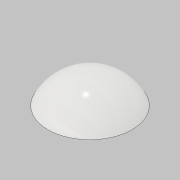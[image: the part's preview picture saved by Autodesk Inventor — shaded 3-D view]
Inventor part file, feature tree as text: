
AUTODESK INVENTOR PART (.ipt)
format: ipt  version: 2019.2 (Build 232265000, 265)  size: 482,816 bytes
history: native  units: mm
features: sketch x4, revolve x3, extrude x2, shell x1, plane x1, other x1, fillet x1
ambient origin geometry x8: Origin, YZ Plane, XZ Plane, XY Plane, X Axis, Y Axis, Z Axis, Center Point
bodies: Volumenkörper1 (feature_tree)
feature tree (13):
  shell  "ShellLower.ipt"  Thickness=10.0mm
  revolve  "Umdrehung1"
  revolve  "Umdrehung2"
  revolve  "Umdrehung3"
  plane  "Arbeitsebene1"
  other  "Trennen1"
  sketch  "Skizze2"  dims[d3=180.0deg d4=-26.0mm d5=46.0mm]
  extrude  "Extrusion1"  Depth=2.0mm
  extrude  "Extrusion2"  [1 undecoded]
  fillet  "Rundung1"  Radius=46.0mm
  sketch  "Skizze1"  dims[d1=120.0mm d2=2.0mm]
  sketch  "Skizze3"  dims[d6=7.0mm]
  sketch  "Skizze4"  dims[d8=40.0mm d10=360.0deg d12=0.0mm d13=0.0mm d14=2.0mm d15=0.0mm d16=3.0mm d17=3.0mm d18=180.0deg d19=3.0mm d20=3.0mm d21=180.0deg d22=0.25mm]
note: 1 required parameter value undecoded (feature->parameter linkage not recoverable at this tier; creation-order binding heuristic only, values carry confidence <= 0.55)
